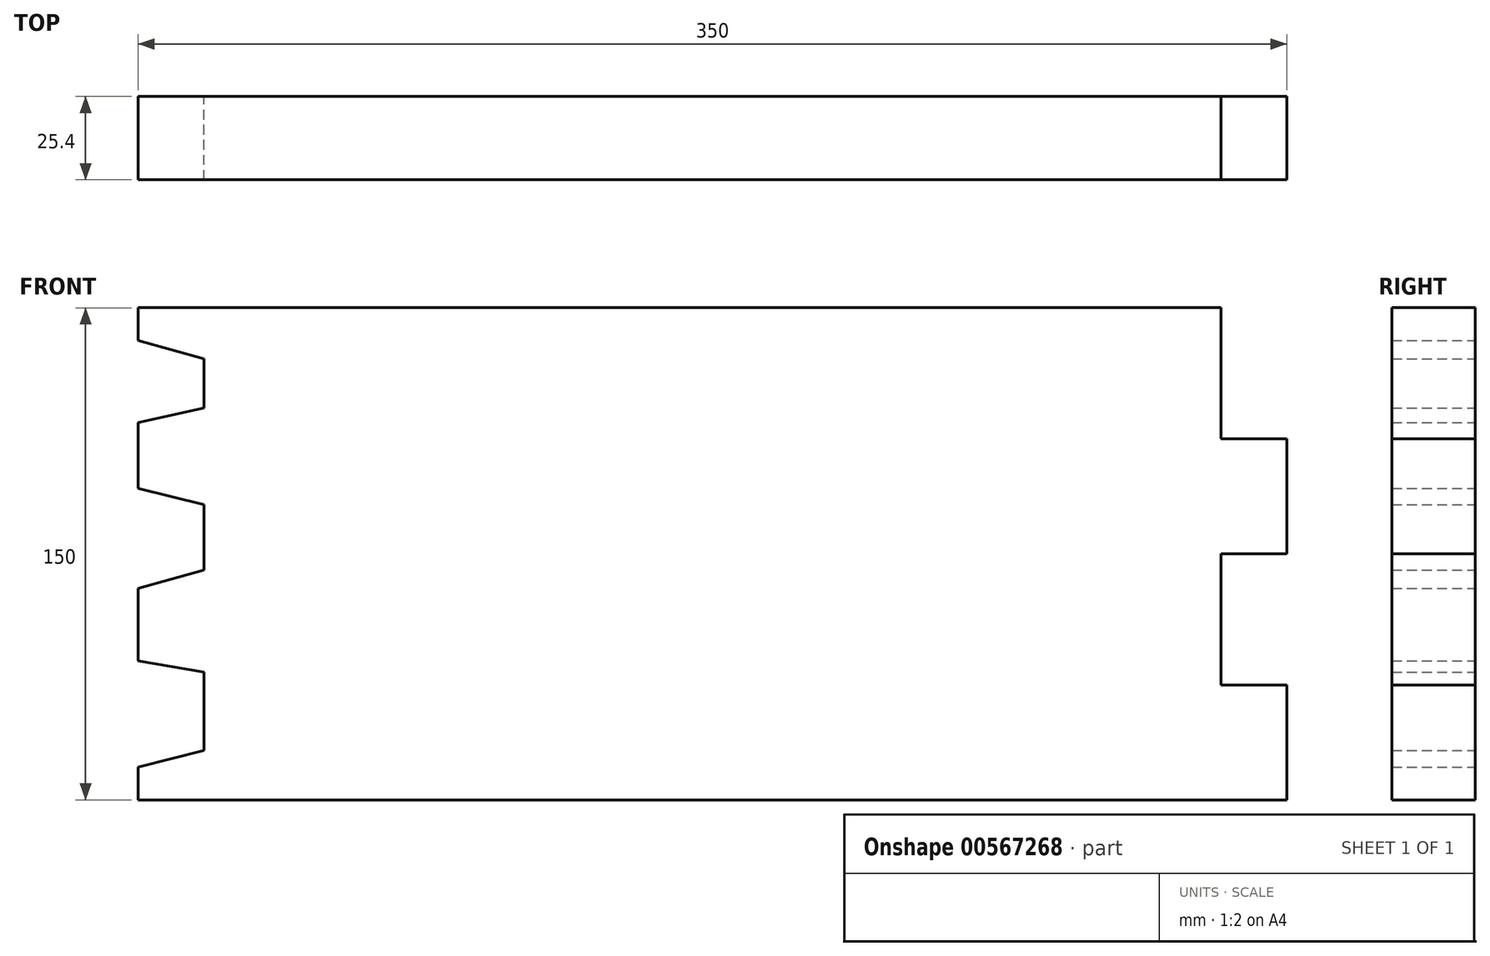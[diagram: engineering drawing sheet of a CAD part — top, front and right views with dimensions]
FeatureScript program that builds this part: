
annotation { "Feature Type Name" : "Feature", "Feature Type Description" : "" }
export const myFeature = defineFeature(function(context is Context, id is Id, definition is map)
    precondition{}
    {
        {
            var Q0;
            Q0=qCreatedBy(makeId("Front.planeOp"),FACE);
            var sketch = newSketch(context, id + "F0", { "sketchPlane" : qUnion([Q0])});
            skLineSegment(sketch, "E0.bottom", {"start": v(-72.58, 98.9) * mm, "end": v(277.42, 98.9) * mm});
            skLineSegment(sketch, "E0.top", {"start": v(-72.58, 248.9) * mm, "end": v(277.42, 248.9) * mm});
            skLineSegment(sketch, "E0.left", {"start": v(-72.58, 98.9) * mm, "end": v(-72.58, 108.9) * mm});
            skLineSegment(sketch, "E0.right", {"start": v(277.42, 98.9) * mm, "end": v(277.42, 133.9) * mm});
            skLineSegment(sketch, "E1", {"start": v(257.42, 248.9) * mm, "end": v(257.42, 98.9) * mm});
            skLineSegment(sketch, "E2", {"start": v(257.42, 173.9) * mm, "end": v(277.42, 173.9) * mm});
            skLineSegment(sketch, "E3", {"start": v(257.42, 133.9) * mm, "end": v(277.42, 133.9) * mm});
            skLineSegment(sketch, "E4", {"start": v(257.42, 208.9) * mm, "end": v(277.42, 208.9) * mm});
            skLineSegment(sketch, "E5.trimOffspring", {"start": v(277.42, 173.9) * mm, "end": v(277.42, 208.9) * mm});
            skLineSegment(sketch, "E6", {"start": v(-52.58, 248.9) * mm, "end": v(-52.58, 98.9) * mm});
            skLineSegment(sketch, "E7", {"start": v(-52.58, 233.3) * mm, "end": v(-72.58, 238.9) * mm});
            skLineSegment(sketch, "E8", {"start": v(-52.58, 218.3) * mm, "end": v(-72.58, 213.9) * mm});
            skLineSegment(sketch, "E9", {"start": v(-52.58, 188.9) * mm, "end": v(-72.58, 193.9) * mm});
            skLineSegment(sketch, "E10", {"start": v(-52.58, 113.9) * mm, "end": v(-72.58, 108.9) * mm});
            skLineSegment(sketch, "E11", {"start": v(-52.58, 137.9) * mm, "end": v(-72.58, 141.32) * mm});
            skLineSegment(sketch, "E12", {"start": v(-52.58, 168.9) * mm, "end": v(-72.58, 163.32) * mm});
            skLineSegment(sketch, "E13.trimOffspring", {"start": v(-72.58, 141.32) * mm, "end": v(-72.58, 163.32) * mm});
            skLineSegment(sketch, "E14.trimOffspring", {"start": v(-72.58, 193.9) * mm, "end": v(-72.58, 213.9) * mm});
            skLineSegment(sketch, "E15.trimOffspring", {"start": v(-72.58, 238.9) * mm, "end": v(-72.58, 248.9) * mm});
            skSolve(sketch);
        }
        {
            var Q0;
            Q0 = qSketchRegion(id + "F0", true);
            extrude(context, id + "F1", {"entities" : qUnion([Q0]), "depth" : 25.4 * mm, "offsetDistance" : 25.4 * mm});
        }
    });
